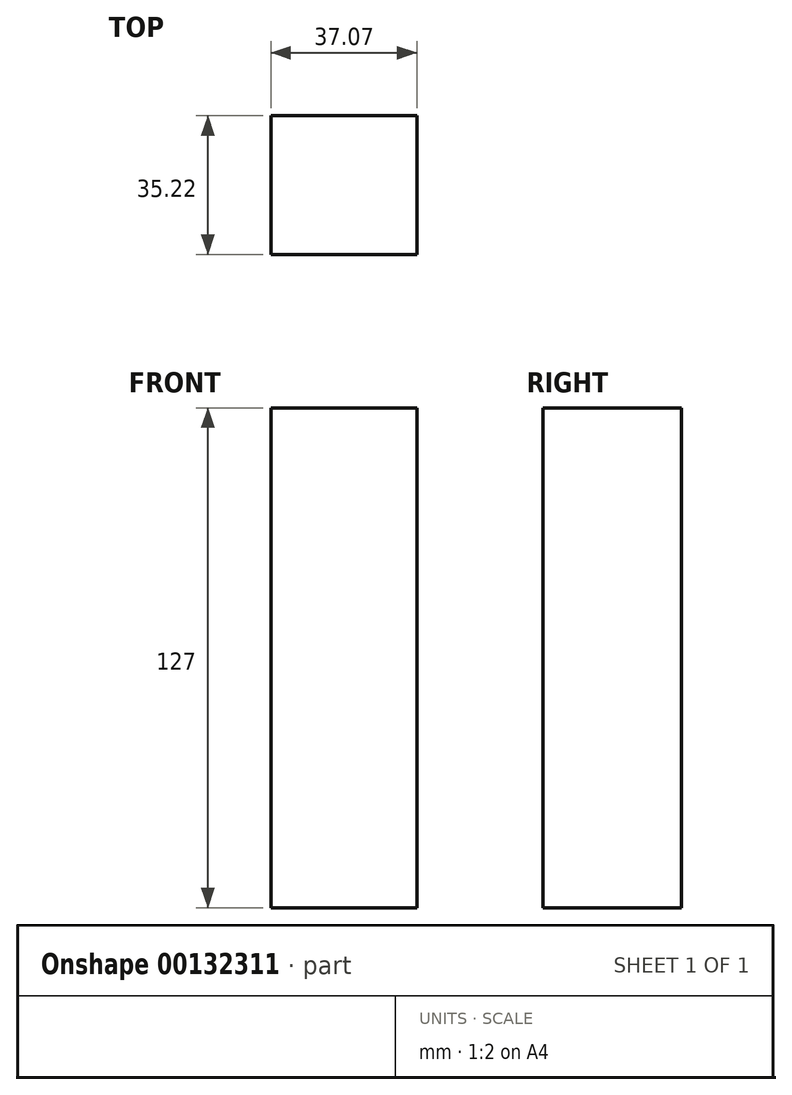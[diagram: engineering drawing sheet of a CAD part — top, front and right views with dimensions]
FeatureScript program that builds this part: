
annotation { "Feature Type Name" : "Feature", "Feature Type Description" : "" }
export const myFeature = defineFeature(function(context is Context, id is Id, definition is map)
    precondition{}
    {
        {
            var Q0;
            Q0=qCreatedBy(makeId("Top.planeOp"),FACE);
            var sketch = newSketch(context, id + "F0", { "sketchPlane" : qUnion([Q0])});
            skLineSegment(sketch, "E0.bottom", {"start": v(-32.75, 26.26) * mm, "end": v(4.32, 26.26) * mm});
            skLineSegment(sketch, "E0.top", {"start": v(-32.75, -8.96) * mm, "end": v(4.32, -8.96) * mm});
            skLineSegment(sketch, "E0.left", {"start": v(-32.75, 26.26) * mm, "end": v(-32.75, -8.96) * mm});
            skLineSegment(sketch, "E0.right", {"start": v(4.32, 26.26) * mm, "end": v(4.32, -8.96) * mm});
            skSolve(sketch);
        }
        {
            var Q0;
            Q0 = qSketchRegion(id + "F0", true);
            extrude(context, id + "F1", {"entities" : qUnion([Q0]), "depth" : 127 * mm});
        }
    });
